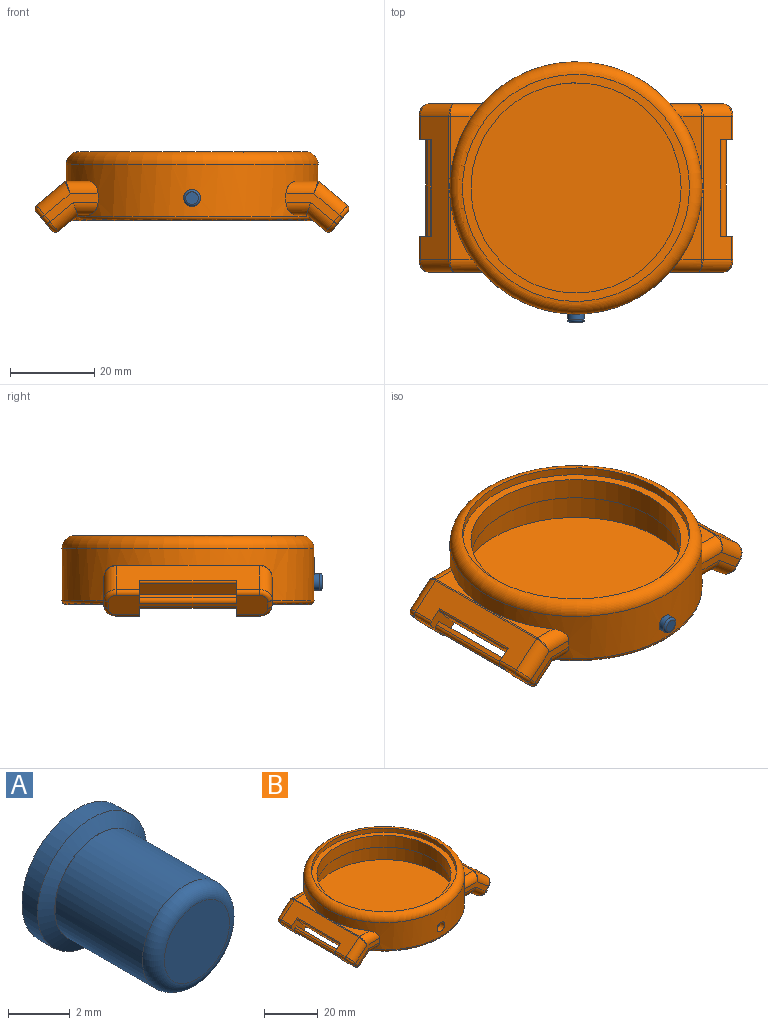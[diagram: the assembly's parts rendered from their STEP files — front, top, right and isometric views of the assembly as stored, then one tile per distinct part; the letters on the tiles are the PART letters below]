
ASSEMBLY  parts=2 mates=1
PART A: 7 faces, bbox 5x5.5x5 mm
  f0: cylinder r=2.5mm len=5mm, axis (0,1,0), area 11.2mm2, adj f2,f6
  f1: plane 4x4mm, normal (0,-1,0), area 0.1mm2, adj f3,f6
  f2: plane 5x5mm, normal (0,1,0), area 19.6mm2, adj f0
  f3: cylinder r=1.99mm len=4mm, axis (0,1,0), area 50mm2, adj f1,f5
  f4: plane 2.98x2.98mm, normal (0,-1,0), area 7mm2, adj f5
  f5: torus R=1.49mm, axis (0,-1,0), area 8.9mm2, adj f3,f4
  f6: cone r=2mm half-angle=60deg, axis (0,1,0), area 8.2mm2, adj f0,f1
PART B: 103 faces, bbox 75x65x19.3 mm
  f0: cylinder r=30mm len=60mm, axis (0,0,-1), area 1619.4mm2, adj f2,f3,f4,f5,f6,f11,f16,f17
  f1: cylinder r=27.5mm len=55mm, axis (0,0,-1), area 1283.3mm2, adj f62,f63,f102
  f2: plane 12.06x4.67mm, normal (0.64,0,-0.77), area 36.2mm2, adj f0,f17,f32,f56,f69,f80,f97
  f3: plane 12.06x4.67mm, normal (-0.64,0,-0.77), area 36.2mm2, adj f0,f25,f36,f48,f73,f80,f92
  f4: plane 14.78x5.2mm, normal (0,0,1), area 27.5mm2, adj f0,f30,f88
  f5: plane 14.78x5.2mm, normal (0,0,1), area 27.5mm2, adj f0,f39,f85
  f6: plane 12.06x4.67mm, normal (0.64,0,-0.77), area 36.2mm2, adj f0,f15,f18,f28,f68,f81,f101
  f7: plane 34x6.77mm, normal (-0.64,0,0.77), area 219.3mm2, adj f14,f31,f35,f55,f68,f69,f79,f88
  f8: plane 38x4.6mm, normal (-0.77,0,-0.64), area 109.6mm2, adj f14,f15,f52,f53,f54,f55,f56,f57
  f9: plane 38x4.6mm, normal (0.77,0,-0.64), area 109.6mm2, adj f12,f13,f44,f45,f46,f47,f48,f49
  f10: plane 34x6.77mm, normal (0.64,0,0.77), area 219.3mm2, adj f12,f38,f40,f47,f72,f73,f78,f83
  f11: plane 12.06x4.67mm, normal (-0.64,0,-0.77), area 36.2mm2, adj f0,f13,f24,f42,f72,f81,f96
  f12: cylinder r=1mm len=5.5mm, axis (0,1,0), area 8.6mm2, adj f9,f10,f49,f72
  f13: cylinder r=1mm len=5.5mm, axis (0,1,0), area 8.6mm2, adj f9,f11,f50,f72
  f14: cylinder r=1mm len=5.5mm, axis (0,1,0), area 8.6mm2, adj f7,f8,f57,f68
  f15: cylinder r=1mm len=5.5mm, axis (0,1,0), area 8.6mm2, adj f6,f8,f58,f68
  f16: plane 14.78x5.2mm, normal (0,0,1), area 27.5mm2, adj f0,f34,f90
  f17: plane 4.32x2.47mm, normal (0,0,-1), area 5mm2, adj f0,f2,f33
  f18: plane 4.32x2.47mm, normal (0,0,-1), area 5mm2, adj f0,f6,f29
  f19: plane 12.71x6.62mm, normal (0,-1,0), area 27.7mm2, adj f0,f32,f33,f34,f35,f52
  f20: plane 12.71x6.62mm, normal (0,1,0), area 27.7mm2, adj f0,f28,f29,f30,f31,f59
  f21: plane 58x57.63mm, normal (0,0,-1), area 2640.5mm2, adj f80,f81,f94,f99
  f22: plane 12.71x6.62mm, normal (0,-1,0), area 27.7mm2, adj f0,f36,f37,f38,f39,f44
  f23: plane 12.71x6.62mm, normal (0,1,0), area 27.7mm2, adj f0,f40,f41,f42,f43,f51
  f24: plane 4.32x2.47mm, normal (0,0,-1), area 5mm2, adj f0,f11,f43
  f25: plane 4.32x2.47mm, normal (0,0,-1), area 5mm2, adj f0,f3,f37
  f26: plane 14.78x5.2mm, normal (0,0,1), area 27.5mm2, adj f0,f41,f83
  f27: torus R=27mm, axis (0,0,1), area 856mm2, adj f0,f61
  f28: cylinder r=3mm len=7.43mm, axis (0.77,0,0.64), area 30.6mm2, adj f6,f20,f29,f58
  f29: cylinder r=3mm len=5.92mm, axis (1,0,0), area 20.4mm2, adj f0,f18,f20,f28
  f30: cylinder r=3mm len=7.56mm, axis (-1,0,0), area 29.8mm2, adj f0,f4,f20,f87
  f31: cylinder r=3mm len=8.68mm, axis (-0.77,0,-0.64), area 40mm2, adj f7,f20,f57,f87
  f32: cylinder r=3mm len=7.43mm, axis (-0.77,0,-0.64), area 30.6mm2, adj f2,f19,f33,f54
  f33: cylinder r=3mm len=5.92mm, axis (-1,0,0), area 20.4mm2, adj f0,f17,f19,f32
  f34: cylinder r=3mm len=7.56mm, axis (1,0,0), area 29.8mm2, adj f0,f16,f19,f91
  f35: cylinder r=3mm len=8.68mm, axis (0.77,0,0.64), area 40mm2, adj f7,f19,f53,f91
  f36: cylinder r=3mm len=7.43mm, axis (-0.77,0,0.64), area 30.6mm2, adj f3,f22,f37,f46
  f37: cylinder r=3mm len=5.92mm, axis (-1,0,0), area 20.4mm2, adj f0,f22,f25,f36
  f38: cylinder r=3mm len=8.68mm, axis (0.77,0,-0.64), area 40mm2, adj f10,f22,f45,f86
  f39: cylinder r=3mm len=7.56mm, axis (1,0,0), area 29.8mm2, adj f0,f5,f22,f86
  f40: cylinder r=3mm len=8.68mm, axis (-0.77,0,0.64), area 40mm2, adj f10,f23,f49,f82
  f41: cylinder r=3mm len=7.56mm, axis (-1,0,0), area 29.8mm2, adj f0,f23,f26,f82
  f42: cylinder r=3mm len=7.43mm, axis (0.77,0,-0.64), area 30.6mm2, adj f11,f23,f43,f50
  f43: cylinder r=3mm len=5.92mm, axis (1,0,0), area 20.4mm2, adj f0,f23,f24,f42
  f44: cylinder r=1mm len=2.18mm, axis (-0.64,0,-0.77), area 3.1mm2, adj f9,f22,f45,f46
  f45: torus R=2mm, axis (0.77,0,-0.64), area 6.5mm2, adj f9,f38,f44,f47
  f46: torus R=2mm, axis (0.77,0,-0.64), area 6.5mm2, adj f9,f36,f44,f48
  f47: cylinder r=1mm len=5.5mm, axis (0,1,0), area 8.6mm2, adj f9,f10,f45,f73
  f48: cylinder r=1mm len=5.5mm, axis (0,1,0), area 8.6mm2, adj f3,f9,f46,f73
  f49: torus R=2mm, axis (0.77,0,-0.64), area 6.5mm2, adj f9,f12,f40,f51
  f50: torus R=2mm, axis (0.77,0,-0.64), area 6.5mm2, adj f9,f13,f42,f51
  f51: cylinder r=1mm len=2.18mm, axis (0.64,0,0.77), area 3.1mm2, adj f9,f23,f49,f50
  f52: cylinder r=1mm len=2.18mm, axis (-0.64,0,0.77), area 3.1mm2, adj f8,f19,f53,f54
  f53: torus R=2mm, axis (0.77,0,0.64), area 6.5mm2, adj f8,f35,f52,f55
  f54: torus R=2mm, axis (0.77,0,0.64), area 6.5mm2, adj f8,f32,f52,f56
  f55: cylinder r=1mm len=5.5mm, axis (0,1,0), area 8.6mm2, adj f7,f8,f53,f69
  f56: cylinder r=1mm len=5.5mm, axis (0,1,0), area 8.6mm2, adj f2,f8,f54,f69
  f57: torus R=2mm, axis (0.77,0,0.64), area 6.5mm2, adj f8,f14,f31,f59
  f58: torus R=2mm, axis (0.77,0,0.64), area 6.5mm2, adj f8,f15,f28,f59
  f59: cylinder r=1mm len=2.18mm, axis (0.64,0,-0.77), area 3.1mm2, adj f8,f20,f57,f58
  f60: plane 54x54mm, normal (0,0,1), area 326.7mm2, adj f61,f64
  f61: cylinder r=27mm len=54mm, axis (0,0,1), area 339.3mm2, adj f27,f60
  f62: plane 55x55mm, normal (0,0,1), area 2375.8mm2, adj f1
  f63: plane 55x55mm, normal (0,0,-1), area 412.3mm2, adj f1,f64
  f64: cylinder r=25mm len=50mm, axis (0,0,1), area 832.5mm2, adj f60,f63
  f65: plane 23x0.77mm, normal (-0.64,0,0.77), area 23mm2, adj f66,f68,f69,f76
  f66: plane 23x1.53mm, normal (0.77,0,0.64), area 46mm2, adj f65,f68,f69,f77
  f67: plane 23x4.98mm, normal (-0.77,0,-0.64), area 149.5mm2, adj f68,f69,f79,f97,f98,f99,f100,f101
  f68: plane 8.61x8.56mm, normal (0,-1,0), area 26.5mm2, adj f6,f7,f8,f14,f15,f65,f66,f67
  f69: plane 8.61x8.56mm, normal (0,1,0), area 26.5mm2, adj f2,f7,f8,f55,f56,f65,f66,f67
  f70: plane 23x0.77mm, normal (-0.77,0,0.64), area 23mm2, adj f72,f73,f74,f75
  f71: plane 23x4.98mm, normal (0.77,0,-0.64), area 149.5mm2, adj f72,f73,f78,f92,f93,f94,f95,f96
  f72: plane 8.61x8.56mm, normal (0,-1,0), area 26.7mm2, adj f9,f10,f11,f12,f13,f70,f71,f74
  f73: plane 8.61x8.56mm, normal (0,1,0), area 26.7mm2, adj f3,f9,f10,f47,f48,f70,f71,f74
  f74: cylinder r=1mm len=23mm, axis (0,1,0), area 72.3mm2, adj f9,f70,f72,f73
  f75: cylinder r=1mm len=23mm, axis (0,1,0), area 72.3mm2, adj f9,f70,f72,f73
  f76: cylinder r=1mm len=23mm, axis (0,1,0), area 36.1mm2, adj f8,f65,f68,f69
  f77: cylinder r=1mm len=23mm, axis (0,1,0), area 72.3mm2, adj f8,f66,f68,f69
  f78: cylinder r=0.5mm len=23mm, axis (0,1,0), area 18.1mm2, adj f10,f71,f72,f73
  f79: cylinder r=0.5mm len=23mm, axis (0,1,0), area 18.1mm2, adj f7,f67,f68,f69
  f80: torus R=29mm, axis (0,0,1), area 120.1mm2, adj f0,f2,f3,f21,f93,f98
  f81: torus R=29mm, axis (0,0,1), area 120.1mm2, adj f0,f6,f11,f21,f95,f100
  f82: bspline ~3.4x3mm, area 1.1mm2, adj f40,f41,f83
  f83: cylinder r=0.5mm len=14.78mm, axis (0,1,0), area 5.2mm2, adj f10,f26,f82,f84
  f84: bspline ~5.27x0.37mm, area 1.3mm2, adj f0,f10,f83,f85
  f85: cylinder r=0.5mm len=14.78mm, axis (0,1,0), area 5.2mm2, adj f5,f10,f84,f86
  f86: bspline ~3.4x3mm, area 1.1mm2, adj f38,f39,f85
  f87: bspline ~3.4x3mm, area 1.1mm2, adj f30,f31,f88
  f88: cylinder r=0.5mm len=14.78mm, axis (0,-1,0), area 5.2mm2, adj f4,f7,f87,f89
  f89: bspline ~6.08x0.42mm, area 1.3mm2, adj f0,f7,f88,f90
  f90: cylinder r=0.5mm len=14.78mm, axis (0,-1,0), area 5.2mm2, adj f7,f16,f89,f91
  f91: bspline ~3.4x3mm, area 1.1mm2, adj f34,f35,f90
  f92: cylinder r=1mm len=6.55mm, axis (0,1,0), area 10.3mm2, adj f3,f71,f73,f93
  f93: bspline ~3.09x1.43mm, area 2.6mm2, adj f71,f80,f92,f94
  f94: cylinder r=1mm len=6.55mm, axis (0,1,0), area 10.1mm2, adj f21,f71,f93,f95
  f95: bspline ~4.45x1.5mm, area 2.6mm2, adj f71,f81,f94,f96
  f96: cylinder r=1mm len=6.55mm, axis (0,1,0), area 10.3mm2, adj f11,f71,f72,f95
  f97: cylinder r=1mm len=6.55mm, axis (0,1,0), area 10.3mm2, adj f2,f67,f69,f98
  f98: bspline ~4.45x1.5mm, area 2.6mm2, adj f67,f80,f97,f99
  f99: cylinder r=1mm len=6.55mm, axis (0,1,0), area 10.1mm2, adj f21,f67,f98,f100
  f100: bspline ~3.09x1.43mm, area 2.6mm2, adj f67,f81,f99,f101
  f101: cylinder r=1mm len=6.55mm, axis (0,1,0), area 10.3mm2, adj f6,f67,f68,f100
  f102: cylinder r=2mm len=4mm, axis (0,1,0), area 31.4mm2, adj f0,f1
PLACE A t=(-1.8,-26.54,-4.15)mm
PLACE B t=(-1.8,-0.13,-0.15)mm
MATE cylindrical A.f0 <-> B.f102  axis (0,1,0) through (-1.8,-27.54,-4.15)mm
